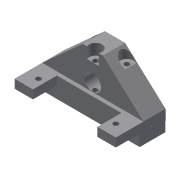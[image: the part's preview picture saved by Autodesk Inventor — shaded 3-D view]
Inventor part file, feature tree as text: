
AUTODESK INVENTOR PART (.ipt)
format: ipt  version: 2019.4 (Build 234330000, 330)  size: 166,400 bytes
history: native  units: mm
features: reference x17, other x7, sketch x4, plane x3, extrude x3, hole x1, projected_geometry x1
ambient origin geometry x8: Origin, YZ Plane, XZ Plane, XY Plane, X Axis, Y Axis, Z Axis, Center Point
bodies: Solid1 (feature_tree)
feature tree (36):
  plane  "Work Plane1"
  sketch  "Sketch1"  dims[d0=11.0mm d1=10.0mm d2=0.0mm]
  plane  "Work Plane2"
  extrude  "Extrusion1"  Depth=10.0mm TaperAngle=0.0deg
  sketch  "Sketch2"  dims[d3=10.0mm d4=4.7mm]
  plane  "Work Plane3"
  extrude  "Extrusion2"  Depth=4.7mm
  extrude  "Extrusion3"  Depth=4.7mm
  hole  "Hole1"  [1 undecoded]
  reference  "Reference1"
  reference  "Reference2"
  reference  "Reference3"
  reference  "Reference4"
  reference  "Reference5"
  reference  "Reference6"
  reference  "Reference7"
  sketch  "Sketch3"  dims[d5=10.0mm d6=4.7mm]
  projected_geometry  "Projected Loop1"
  reference  "Reference8"
  reference  "Reference9"
  sketch  "Sketch4"  dims[d7=10.0mm d8=0.0mm d9=12.0mm d10=0.0mm d11=2.8mm d12=6.0mm d13=7.0mm d14=6.0mm d15=90.0deg d16=8.0mm d17=20.594885mm]
  reference  "Reference10"
  reference  "Reference11"
  reference  "Reference12"
  reference  "Reference13"
  reference  "Reference14"
  reference  "Reference15"
  reference  "Reference16"
  reference  "Reference17"
  other  "Assembly_opentrons_microscope_slide_y.iam"
  other  "00_MGN12H, LINEAR GUIDE BLOCK:2"
  other  "00_spindel_bearings:1"
  other  "01_Slide_camera_y_v0:1"
  other  "00_MGN12 LINEAR GUIDE RAIL, CONFIGURABLE:1"
  other  "00_NEMA11:1"
  other  "Lagerschild_11_1"
note: 1 required parameter value undecoded (feature->parameter linkage not recoverable at this tier; creation-order binding heuristic only, values carry confidence <= 0.55)
